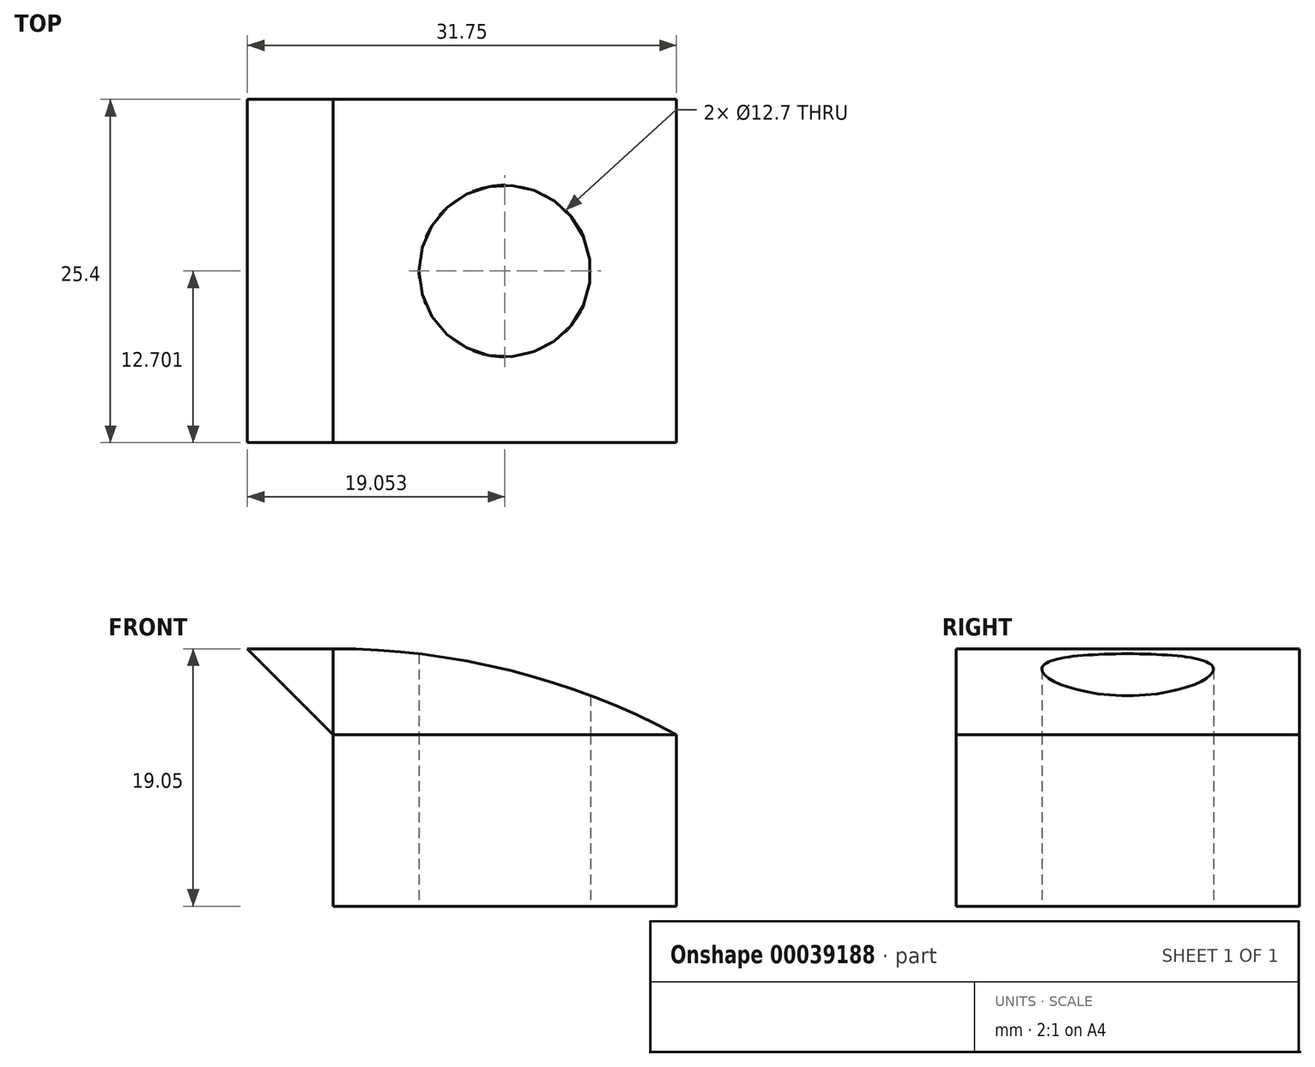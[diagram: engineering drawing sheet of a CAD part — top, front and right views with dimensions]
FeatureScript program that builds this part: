
annotation { "Feature Type Name" : "Feature", "Feature Type Description" : "" }
export const myFeature = defineFeature(function(context is Context, id is Id, definition is map)
    precondition{}
    {
        {
            var Q0;
            Q0=qCreatedBy(makeId("Top.planeOp"),FACE);
            var sketch = newSketch(context, id + "F0", { "sketchPlane" : qUnion([Q0])});
            skLineSegment(sketch, "E0.bottom", {"start": v(-11.59, -1.6) * mm, "end": v(13.81, -1.6) * mm});
            skLineSegment(sketch, "E0.top", {"start": v(-11.59, -27) * mm, "end": v(13.81, -27) * mm});
            skLineSegment(sketch, "E0.left", {"start": v(-11.59, -1.6) * mm, "end": v(-11.59, -27) * mm});
            skLineSegment(sketch, "E0.right", {"start": v(13.81, -1.6) * mm, "end": v(13.81, -27) * mm});
            skCircle(sketch, "E1", {"center": v(1.11, -14.3) * mm, "radius": 6.35 * mm});
            skPoint(sketch, "E1.centerSnap0", {"position": v(1.11, -27) * mm});
            skPoint(sketch, "E1.centerSnap1", {"position": v(13.81, -14.3) * mm});
            skSolve(sketch);
        }
        {
            var Q0;
            Q0 = qSketchRegion(id + "F0", true);
            extrude(context, id + "F1", {"entities" : qUnion([Q0]), "depth" : 12.7 * mm});
        }
        {
            var Q0;
            Q0=makeQuery(id+"F1.opExtrude","CAP_FACE",FACE,{"disambiguationData":[OSD([sQuery(id+"F0.wireOp",EDGE,"E0.bottom"),sQuery(id+"F0.wireOp",EDGE,"E0.top"),sQuery(id+"F0.wireOp",EDGE,"E0.left"),sQuery(id+"F0.wireOp",EDGE,"E0.right"),sQuery(id+"F0.wireOp",EDGE,"E1")])],"isStart":false});
            extrude(context, id + "F2", {"entities" : qUnion([Q0]), "depth" : 6.35 * mm});
        }
        {
            var Q0;
            Q0=makeQuery(id+"F2.opExtrude","SWEPT_FACE",FACE,{"disambiguationData":[OSD([sQuery(id+"F0.wireOp",EDGE,"E0.left")])]});
            extrude(context, id + "F3", {"entities" : qUnion([Q0]), "depth" : 6.35 * mm});
        }
        {
            var Q0;
            Q0=makeQuery(id+"F3.opExtrude","SWEPT_FACE",FACE,{"disambiguationData":[OSD([sQuery(id+"F0.wireOp",EDGE,"E0.bottom"),sQuery(id+"F0.wireOp",EDGE,"E0.left")])]});
            var sketch = newSketch(context, id + "F4", { "sketchPlane" : qUnion([Q0])});
            skLineSegment(sketch, "E2", {"start": v(11.59, 12.7) * mm, "end": v(17.94, 19.05) * mm});
            skSolve(sketch);
        }
        {
            var Q0;
            Q0 = qSketchRegion(id + "F4", true);
            var Q1;
            Q1=makeQuery(id+"F4.imprint","IMPRINT",FACE,{"disambiguationData":[TD([[makeQuery(id+"F4.imprint","IMPRINT",EDGE,{"derivedFrom":sQuery(id+"F4.wireOp",EDGE,"E2")}),-1.0]])]});
            extrude(context, id + "F5", {"entities" : qUnion([Q0, Q1]), "operationType" : NewBodyOperationType.REMOVE, "oppositeDirection" : true, "depth" : 25.4 * mm});
        }
        {
            var Q0;
            Q0=makeQuery(id+"F2.opExtrude","SWEPT_FACE",FACE,{"disambiguationData":[OSD([sQuery(id+"F0.wireOp",EDGE,"E0.bottom")])]});
            var sketch = newSketch(context, id + "F6", { "sketchPlane" : qUnion([Q0])});
            skArc(sketch, "E3", {"start": v(11.59, 19.05) * mm, "mid": v(-1.5, 17.44) * mm, "end": v(-13.81, 12.7) * mm});
            skSolve(sketch);
        }
        {
            var Q0;
            Q0 = qSketchRegion(id + "F6", true);
            var Q1;
            Q1=makeQuery(id+"F6.imprint","IMPRINT",FACE,{"disambiguationData":[TD([[makeQuery(id+"F6.imprint","IMPRINT",EDGE,{"derivedFrom":sQuery(id+"F6.wireOp",EDGE,"E3")}),-1.0]])]});
            extrude(context, id + "F7", {"entities" : qUnion([Q0, Q1]), "operationType" : NewBodyOperationType.REMOVE, "oppositeDirection" : true, "depth" : 25.4 * mm});
        }
    });
